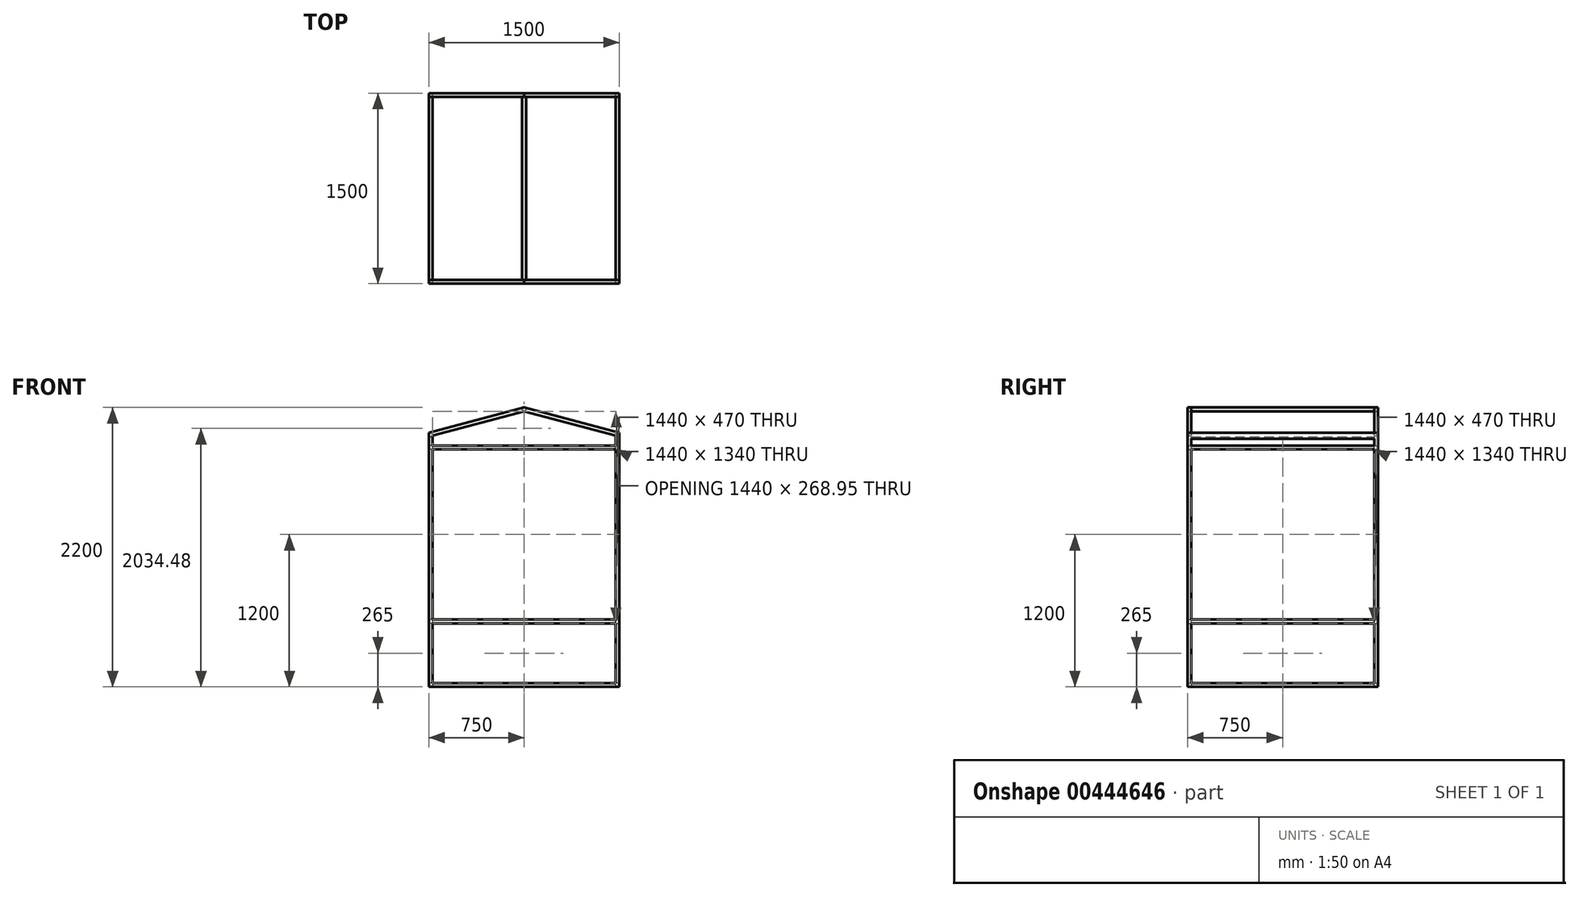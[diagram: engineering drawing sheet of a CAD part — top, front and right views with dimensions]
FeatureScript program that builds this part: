
annotation { "Feature Type Name" : "Feature", "Feature Type Description" : "" }
export const myFeature = defineFeature(function(context is Context, id is Id, definition is map)
    precondition{}
    {
        {
            var Q0;
            Q0=qCreatedBy(makeId("Front.planeOp"),FACE);
            var sketch = newSketch(context, id + "F0", { "sketchPlane" : qUnion([Q0])});
            skLineSegment(sketch, "E0.bottom", {"start": v(30, 0) * mm, "end": v(1470, 0) * mm});
            skLineSegment(sketch, "E0.left", {"start": v(0, 0) * mm, "end": v(0, 1500) * mm});
            skLineSegment(sketch, "E0.right", {"start": v(1500, 0) * mm, "end": v(1500, 1500) * mm});
            skLineSegment(sketch, "E1.0", {"start": v(30, 30) * mm, "end": v(30, 1370) * mm});
            skLineSegment(sketch, "E1.1", {"start": v(30, 30) * mm, "end": v(1470, 30) * mm});
            skLineSegment(sketch, "E1.2", {"start": v(1470, 30) * mm, "end": v(1470, 1370) * mm});
            skLineSegment(sketch, "E2.top", {"start": v(0, -500) * mm, "end": v(30, -500) * mm});
            skLineSegment(sketch, "E2.left", {"start": v(0, 0) * mm, "end": v(0, -500) * mm});
            skLineSegment(sketch, "E2.right", {"start": v(30, 0) * mm, "end": v(30, -500) * mm});
            skLineSegment(sketch, "E3.top", {"start": v(1500, -500) * mm, "end": v(1470, -500) * mm});
            skLineSegment(sketch, "E3.left", {"start": v(1500, 0) * mm, "end": v(1500, -500) * mm});
            skLineSegment(sketch, "E3.right", {"start": v(1470, 0) * mm, "end": v(1470, -500) * mm});
            skLineSegment(sketch, "E4", {"start": v(0, 1500) * mm, "end": v(750, 1700) * mm});
            skLineSegment(sketch, "E5", {"start": v(750, 1700) * mm, "end": v(1500, 1500) * mm});
            skLineSegment(sketch, "E6.0", {"start": v(750, 1668.95) * mm, "end": v(1470, 1476.95) * mm});
            skLineSegment(sketch, "E6.1", {"start": v(30, 1476.95) * mm, "end": v(750, 1668.95) * mm});
            skLineSegment(sketch, "E7.bottom", {"start": v(30, -500) * mm, "end": v(1470, -500) * mm});
            skLineSegment(sketch, "E7.top", {"start": v(30, -470) * mm, "end": v(1470, -470) * mm});
            skLineSegment(sketch, "E7.left", {"start": v(30, -500) * mm, "end": v(30, -470) * mm});
            skLineSegment(sketch, "E7.right", {"start": v(1470, -500) * mm, "end": v(1470, -470) * mm});
            skLineSegment(sketch, "E8.bottom", {"start": v(30, -470) * mm, "end": v(0, -470) * mm});
            skLineSegment(sketch, "E8.top", {"start": v(30, -500) * mm, "end": v(0, -500) * mm});
            skLineSegment(sketch, "E8.left", {"start": v(30, -470) * mm, "end": v(30, -500) * mm});
            skLineSegment(sketch, "E8.right", {"start": v(0, -470) * mm, "end": v(0, -500) * mm});
            skLineSegment(sketch, "E9.bottom", {"start": v(30, 1400) * mm, "end": v(1470, 1400) * mm});
            skLineSegment(sketch, "E9.top", {"start": v(30, 1370) * mm, "end": v(1470, 1370) * mm});
            skLineSegment(sketch, "E10.trimOffspring", {"start": v(30, 1400) * mm, "end": v(30, 1476.95) * mm});
            skLineSegment(sketch, "E11.trimOffspring", {"start": v(1470, 1400) * mm, "end": v(1470, 1476.95) * mm});
            skSolve(sketch);
        }
        {
            var Q0;
            Q0 = qSketchRegion(id + "F0", true);
            extrude(context, id + "F1", {"entities" : qUnion([Q0]), "depth" : 30 * mm});
        }
        {
            var Q0;
            Q0=makeQuery(id+"F1.opExtrude","CAP_FACE",FACE,{"disambiguationData":[OSD([sQuery(id+"F0.wireOp",EDGE,"E0.bottom"),sQuery(id+"F0.wireOp",EDGE,"E0.left"),sQuery(id+"F0.wireOp",EDGE,"E0.right"),sQuery(id+"F0.wireOp",EDGE,"E1.0"),sQuery(id+"F0.wireOp",EDGE,"E1.1"),sQuery(id+"F0.wireOp",EDGE,"E1.2"),sQuery(id+"F0.wireOp",EDGE,"E2.left"),sQuery(id+"F0.wireOp",EDGE,"E2.right"),sQuery(id+"F0.wireOp",EDGE,"E3.top"),sQuery(id+"F0.wireOp",EDGE,"E3.left"),sQuery(id+"F0.wireOp",EDGE,"E3.right"),sQuery(id+"F0.wireOp",EDGE,"E4"),sQuery(id+"F0.wireOp",EDGE,"E5"),sQuery(id+"F0.wireOp",EDGE,"E6.0"),sQuery(id+"F0.wireOp",EDGE,"E6.1"),sQuery(id+"F0.wireOp",EDGE,"E7.bottom"),sQuery(id+"F0.wireOp",EDGE,"E7.top"),sQuery(id+"F0.wireOp",EDGE,"E8.top"),sQuery(id+"F0.wireOp",EDGE,"E8.right"),sQuery(id+"F0.wireOp",EDGE,"E9.bottom"),sQuery(id+"F0.wireOp",EDGE,"E9.top"),sQuery(id+"F0.wireOp",EDGE,"E10.trimOffspring"),sQuery(id+"F0.wireOp",EDGE,"E11.trimOffspring")])],"isStart":false});
            var sketch = newSketch(context, id + "F2", { "sketchPlane" : qUnion([Q0])});
            skLineSegment(sketch, "E12.bottom", {"start": v(0, 1500) * mm, "end": v(30, 1500) * mm});
            skLineSegment(sketch, "E12.top", {"start": v(0, 1470) * mm, "end": v(30, 1470) * mm});
            skLineSegment(sketch, "E12.left", {"start": v(0, 1500) * mm, "end": v(0, 1470) * mm});
            skLineSegment(sketch, "E12.right", {"start": v(30, 1500) * mm, "end": v(30, 1470) * mm});
            skLineSegment(sketch, "E13.bottom", {"start": v(1500, 1500) * mm, "end": v(1470, 1500) * mm});
            skLineSegment(sketch, "E13.top", {"start": v(1500, 1454.2) * mm, "end": v(1470, 1454.2) * mm});
            skLineSegment(sketch, "E13.left", {"start": v(1500, 1500) * mm, "end": v(1500, 1454.2) * mm});
            skLineSegment(sketch, "E13.right", {"start": v(1470, 1500) * mm, "end": v(1470, 1454.2) * mm});
            skLineSegment(sketch, "E14.bottom", {"start": v(30, 1370) * mm, "end": v(0, 1370) * mm});
            skLineSegment(sketch, "E14.top", {"start": v(30, 1400) * mm, "end": v(0, 1400) * mm});
            skLineSegment(sketch, "E14.left", {"start": v(30, 1370) * mm, "end": v(30, 1400) * mm});
            skLineSegment(sketch, "E14.right", {"start": v(0, 1370) * mm, "end": v(0, 1400) * mm});
            skLineSegment(sketch, "E15.bottom", {"start": v(1470, 1370) * mm, "end": v(1500, 1370) * mm});
            skLineSegment(sketch, "E15.top", {"start": v(1470, 1400) * mm, "end": v(1500, 1400) * mm});
            skLineSegment(sketch, "E15.left", {"start": v(1470, 1370) * mm, "end": v(1470, 1400) * mm});
            skLineSegment(sketch, "E15.right", {"start": v(1500, 1370) * mm, "end": v(1500, 1400) * mm});
            skLineSegment(sketch, "E16.bottom", {"start": v(30, 0) * mm, "end": v(0, 0) * mm});
            skLineSegment(sketch, "E16.top", {"start": v(30, 30) * mm, "end": v(0, 30) * mm});
            skLineSegment(sketch, "E16.left", {"start": v(30, 0) * mm, "end": v(30, 30) * mm});
            skLineSegment(sketch, "E16.right", {"start": v(0, 0) * mm, "end": v(0, 30) * mm});
            skLineSegment(sketch, "E17.bottom", {"start": v(30, -470) * mm, "end": v(0, -470) * mm});
            skLineSegment(sketch, "E17.top", {"start": v(30, -500) * mm, "end": v(0, -500) * mm});
            skLineSegment(sketch, "E17.left", {"start": v(30, -470) * mm, "end": v(30, -500) * mm});
            skLineSegment(sketch, "E17.right", {"start": v(0, -470) * mm, "end": v(0, -500) * mm});
            skLineSegment(sketch, "E18.bottom", {"start": v(1470, 0) * mm, "end": v(1500, 0) * mm});
            skLineSegment(sketch, "E18.top", {"start": v(1470, 30) * mm, "end": v(1500, 30) * mm});
            skLineSegment(sketch, "E18.left", {"start": v(1470, 0) * mm, "end": v(1470, 30) * mm});
            skLineSegment(sketch, "E18.right", {"start": v(1500, 0) * mm, "end": v(1500, 30) * mm});
            skLineSegment(sketch, "E19.bottom", {"start": v(1500, -500) * mm, "end": v(1470, -500) * mm});
            skLineSegment(sketch, "E19.top", {"start": v(1500, -470) * mm, "end": v(1470, -470) * mm});
            skLineSegment(sketch, "E19.left", {"start": v(1500, -500) * mm, "end": v(1500, -470) * mm});
            skLineSegment(sketch, "E19.right", {"start": v(1470, -500) * mm, "end": v(1470, -470) * mm});
            skCircle(sketch, "E20", {"center": v(750, 1684.6) * mm, "radius": 15.4 * mm});
            skSolve(sketch);
        }
        {
            var Q0;
            Q0 = qSketchRegion(id + "F2", true);
            extrude(context, id + "F3", {"entities" : qUnion([Q0]), "operationType" : NewBodyOperationType.ADD, "depth" : 1440 * mm});
        }
        {
            var Q0;
            Q0=makeQuery(id+"F3.opExtrude","CAP_FACE",FACE,{"disambiguationData":[OSD([sQuery(id+"F2.wireOp",EDGE,"E16.bottom"),sQuery(id+"F2.wireOp",EDGE,"E16.top"),sQuery(id+"F2.wireOp",EDGE,"E16.left"),sQuery(id+"F2.wireOp",EDGE,"E16.right")])],"isStart":false});
            var sketch = newSketch(context, id + "F4", { "sketchPlane" : qUnion([Q0])});
            skLineSegment(sketch, "E21.bottom", {"start": v(0, 0) * mm, "end": v(1500, 0) * mm});
            skLineSegment(sketch, "E21.top", {"start": v(0, -500) * mm, "end": v(1500, -500) * mm});
            skLineSegment(sketch, "E21.left", {"start": v(0, 0) * mm, "end": v(0, -500) * mm});
            skLineSegment(sketch, "E21.right", {"start": v(1500, 0) * mm, "end": v(1500, -500) * mm});
            skLineSegment(sketch, "E22.top", {"start": v(0, 1500) * mm, "end": v(30, 1500) * mm});
            skLineSegment(sketch, "E22.left", {"start": v(0, 0) * mm, "end": v(0, 1500) * mm});
            skLineSegment(sketch, "E22.right", {"start": v(1500, 0) * mm, "end": v(1500, 1500) * mm});
            skLineSegment(sketch, "E23.0", {"start": v(1470, 0) * mm, "end": v(1470, -470) * mm});
            skLineSegment(sketch, "E23.1", {"start": v(30, -470) * mm, "end": v(1470, -470) * mm});
            skLineSegment(sketch, "E23.2", {"start": v(30, 0) * mm, "end": v(30, -470) * mm});
            skLineSegment(sketch, "E24.0", {"start": v(30, 30) * mm, "end": v(30, 1370) * mm});
            skLineSegment(sketch, "E24.1", {"start": v(30, 30) * mm, "end": v(1470, 30) * mm});
            skLineSegment(sketch, "E24.2", {"start": v(1470, 30) * mm, "end": v(1470, 1370) * mm});
            skLineSegment(sketch, "E25.trimOffspring", {"start": v(1470, 1500) * mm, "end": v(1500, 1500) * mm});
            skLineSegment(sketch, "E26.bottom", {"start": v(30, 1400) * mm, "end": v(1470, 1400) * mm});
            skLineSegment(sketch, "E26.top", {"start": v(30, 1370) * mm, "end": v(1470, 1370) * mm});
            skLineSegment(sketch, "E27", {"start": v(0, 1500) * mm, "end": v(750, 1700) * mm});
            skLineSegment(sketch, "E28", {"start": v(750, 1700) * mm, "end": v(1500, 1500) * mm});
            skLineSegment(sketch, "E29.0", {"start": v(750, 1668.95) * mm, "end": v(1492.27, 1471.01) * mm});
            skLineSegment(sketch, "E29.1", {"start": v(7.73, 1471.01) * mm, "end": v(750, 1668.95) * mm});
            skLineSegment(sketch, "E30.trimOffspring", {"start": v(30, 1400) * mm, "end": v(30, 1500) * mm});
            skLineSegment(sketch, "E31.trimOffspring", {"start": v(1470, 1400) * mm, "end": v(1470, 1500) * mm});
            skSolve(sketch);
        }
        {
            var Q0;
            Q0 = qSketchRegion(id + "F4", true);
            extrude(context, id + "F5", {"entities" : qUnion([Q0]), "operationType" : NewBodyOperationType.ADD, "depth" : 30 * mm});
        }
    });
